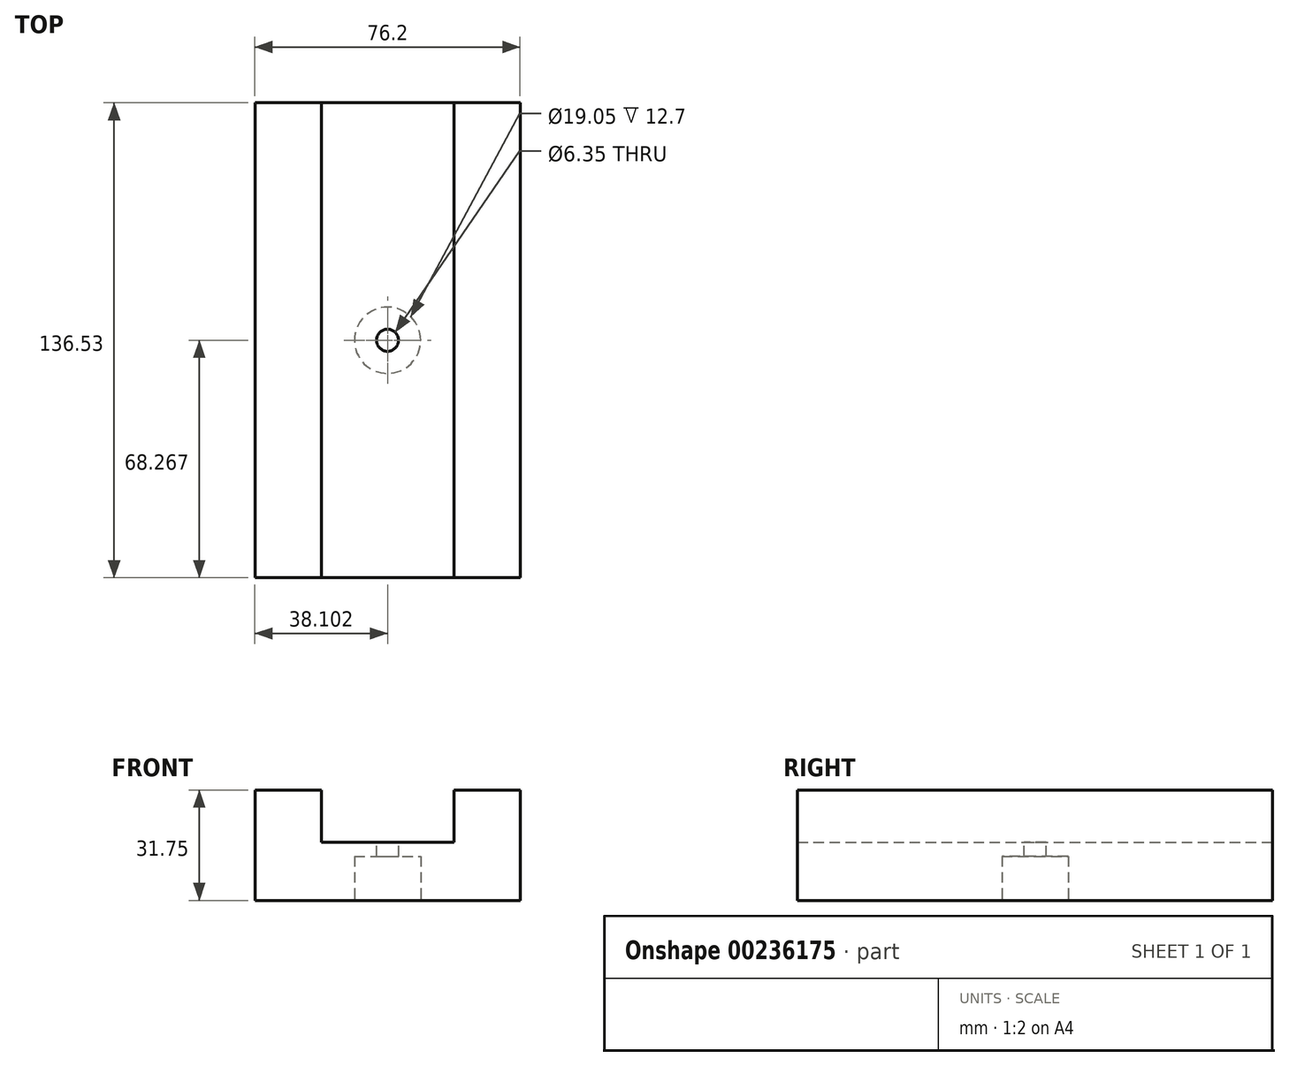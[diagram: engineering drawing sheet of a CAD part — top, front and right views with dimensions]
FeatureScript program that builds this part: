
annotation { "Feature Type Name" : "Feature", "Feature Type Description" : "" }
export const myFeature = defineFeature(function(context is Context, id is Id, definition is map)
    precondition{}
    {
        {
            var Q0;
            Q0=qCreatedBy(makeId("Front.planeOp"),FACE);
            var sketch = newSketch(context, id + "F0", { "sketchPlane" : qUnion([Q0])});
            skLineSegment(sketch, "E0", {"start": v(-48.17, -42.23) * mm, "end": v(28.03, -42.23) * mm});
            skLineSegment(sketch, "E1", {"start": v(28.03, -42.23) * mm, "end": v(28.03, -10.48) * mm});
            skLineSegment(sketch, "E2", {"start": v(-48.17, -42.23) * mm, "end": v(-48.17, -10.48) * mm});
            skLineSegment(sketch, "E3", {"start": v(-48.17, -10.48) * mm, "end": v(-29.12, -10.48) * mm});
            skLineSegment(sketch, "E4", {"start": v(-29.12, -10.48) * mm, "end": v(-29.12, -25.55) * mm});
            skLineSegment(sketch, "E5", {"start": v(-29.12, -25.55) * mm, "end": v(8.98, -25.55) * mm});
            skLineSegment(sketch, "E6", {"start": v(8.98, -25.55) * mm, "end": v(8.98, -10.48) * mm});
            skLineSegment(sketch, "E7", {"start": v(8.98, -10.48) * mm, "end": v(28.03, -10.48) * mm});
            skSolve(sketch);
        }
        {
            var Q0;
            Q0=makeQuery(id+"F0.imprint","IMPRINT",FACE,{"disambiguationData":[TD([[makeQuery(id+"F0.imprint","IMPRINT",EDGE,{"derivedFrom":sQuery(id+"F0.wireOp",EDGE,"E0")}),1.0]])]});
            extrude(context, id + "F1", {"entities" : qUnion([Q0]), "depth" : 136.53 * mm});
        }
        {
            var Q0;
            Q0=makeQuery(id+"F1.opExtrude","SWEPT_FACE",FACE,{"disambiguationData":[OSD([sQuery(id+"F0.wireOp",EDGE,"E5")])]});
            var sketch = newSketch(context, id + "F2", { "sketchPlane" : qUnion([Q0])});
            skPoint(sketch, "E8.centerSnap0", {"position": v(-10.07, 0) * mm});
            skPoint(sketch, "E9.centerSnap0", {"position": v(8.98, -68.26) * mm});
            skCircle(sketch, "E10", {"center": v(-10.07, -68.26) * mm, "radius": 3.18 * mm});
            skSolve(sketch);
        }
        {
            var Q0;
            Q0=makeQuery(id+"F2.imprint","IMPRINT",FACE,{"disambiguationData":[TD([[makeQuery(id+"F2.imprint","IMPRINT",EDGE,{"derivedFrom":sQuery(id+"F2.wireOp",EDGE,"E10")}),1.0]])]});
            extrude(context, id + "F3", {"entities" : qUnion([Q0]), "operationType" : NewBodyOperationType.ADD, "oppositeDirection" : true, "depth" : 6.35 * mm});
        }
        {
            var Q0;
            Q0=makeQuery(id+"F1.opExtrude","SWEPT_FACE",FACE,{"disambiguationData":[OSD([sQuery(id+"F0.wireOp",EDGE,"E5")])]});
            var sketch = newSketch(context, id + "F4", { "sketchPlane" : qUnion([Q0])});
            skCircle(sketch, "E11", {"center": v(-10.07, -68.26) * mm, "radius": 3.18 * mm});
            skPoint(sketch, "E11.centerSnap0", {"position": v(8.98, -68.26) * mm});
            skPoint(sketch, "E11.centerSnap1", {"position": v(-10.07, 0) * mm});
            skSolve(sketch);
        }
        {
            var Q0;
            Q0=makeQuery(id+"F1.opExtrude","SWEPT_FACE",FACE,{"disambiguationData":[OSD([sQuery(id+"F0.wireOp",EDGE,"E0")])]});
            var sketch = newSketch(context, id + "F5", { "sketchPlane" : qUnion([Q0])});
            skCircle(sketch, "E12", {"center": v(-10.07, 68.26) * mm, "radius": 9.53 * mm});
            skPoint(sketch, "E12.centerSnap0", {"position": v(-10.07, 136.53) * mm});
            skPoint(sketch, "E12.centerSnap1", {"position": v(28.03, 68.26) * mm});
            skSolve(sketch);
        }
        {
            var Q0;
            Q0 = qSketchRegion(id + "F5", true);
            extrude(context, id + "F6", {"entities" : qUnion([Q0]), "operationType" : NewBodyOperationType.REMOVE, "oppositeDirection" : true, "depth" : 12.7 * mm});
        }
        {
            var Q0;
            Q0 = qSketchRegion(id + "F4", true);
            extrude(context, id + "F7", {"entities" : qUnion([Q0]), "operationType" : NewBodyOperationType.REMOVE, "oppositeDirection" : true, "depth" : 25.4 * mm});
        }
    });
